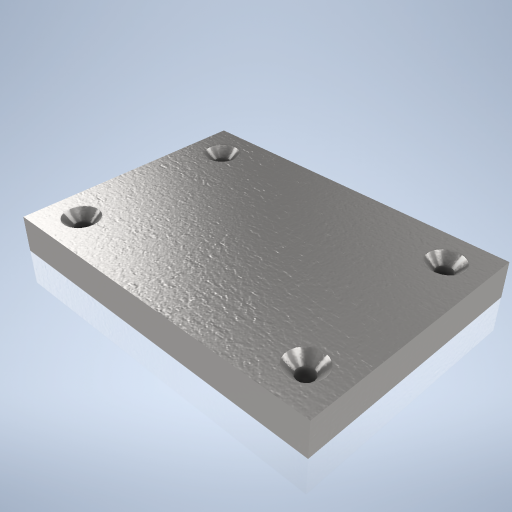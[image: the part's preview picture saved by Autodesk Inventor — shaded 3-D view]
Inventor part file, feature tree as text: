
AUTODESK INVENTOR PART (.ipt)
format: ipt  version: 2024.2 (Build 282272000, 272)  size: 329,216 bytes
history: native  units: mm
features: sketch x2, extrude x1, hole x1, plane x1
ambient origin geometry x8: Origin, YZ Plane, XZ Plane, XY Plane, X Axis, Y Axis, Z Axis, Center Point
bodies: Volumenkörper1 (feature_tree)
feature tree (5):
  extrude  "Extrusion1"  Depth=20.0mm
  hole  "Bohrung1"  [1 undecoded]
  plane  "Arbeitsebene1"
  sketch  "Skizze1"  dims[d0=28.0mm d1=20.0mm]
  sketch  "Skizze2"  dims[d2=3.0mm d3=0.0mm d4=14.0mm d5=3.0mm d6=1.4mm d7=6.0mm d8=3.0mm d9=2.0mm d10=90.0deg d11=8.0mm d12=20.594885mm d13=14.0mm d14=3.0mm]
note: 1 required parameter value undecoded (feature->parameter linkage not recoverable at this tier; creation-order binding heuristic only, values carry confidence <= 0.55)
